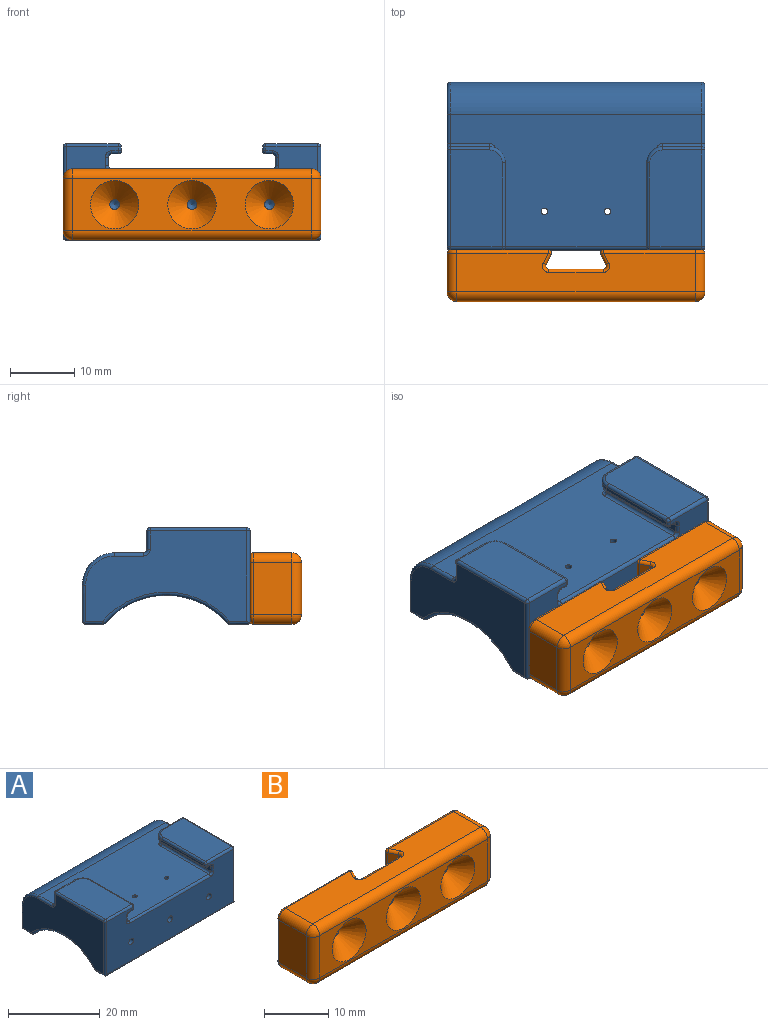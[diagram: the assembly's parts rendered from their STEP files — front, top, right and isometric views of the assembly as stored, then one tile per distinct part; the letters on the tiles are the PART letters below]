
ASSEMBLY  parts=2 mates=1
PART A: 152 faces, bbox 40x26.4x15.3 mm
  f0: cylinder r=2.5mm len=2.5mm, axis (0,0,-1), area 2.6mm2, adj f11,f18,f89,f99,f103
  f1: plane 12.56x0.75mm, normal (0,0,-1), area 9.5mm2, adj f2,f3,f47,f81
  f2: cylinder r=0.5mm len=17.92mm, axis (-1,0,0), area 13.6mm2, adj f1,f4,f26,f41,f42,f47,f49,f83
  f3: cylinder r=0.5mm len=12.56mm, axis (-1,0,0), area 5.8mm2, adj f1,f28,f47,f79
  f4: plane 2.66x0.5mm, normal (0,0,-1), area 1.3mm2, adj f2,f42,f48,f49
  f5: plane 12.56x0.75mm, normal (0,0,-1), area 9.5mm2, adj f43,f44,f46,f78
  f6: plane 2.66x0.5mm, normal (0,0,-1), area 1.3mm2, adj f58,f68,f69,f73
  f7: plane 29x0.75mm, normal (0,0,-1), area 21.8mm2, adj f63,f64,f71,f73
  f8: plane 2.66x0.5mm, normal (0,0,-1), area 1.3mm2, adj f66,f67,f72,f73
  f9: plane 2.66x0.5mm, normal (0,0,-1), area 1.3mm2, adj f40,f44,f45,f50
  f10: cylinder r=12.5mm len=18.92mm, axis (1,0,0), area 107.3mm2, adj f48,f56,f60,f66
  f11: plane 6.05x2.9mm, normal (0,1,0), area 17.5mm2, adj f0,f88,f96,f102,f105
  f12: plane 14.73x1mm, normal (0,0,-1), area 14.2mm2, adj f113,f118,f124,f125
  f13: plane 13x0.6mm, normal (1,0,0), area 7.8mm2, adj f25,f110,f118,f119
  f14: plane 15x8.05mm, normal (0,0,1), area 119.9mm2, adj f119,f120,f126,f130,f131
  f15: plane 25x14mm, normal (-1,0,0), area 245.5mm2, adj f49,f56,f67,f121,f131,f132,f136,f138
  f16: plane 25x14mm, normal (1,0,0), area 245.5mm2, adj f50,f57,f68,f85,f86,f87,f91,f95
  f17: plane 15x8.05mm, normal (0,0,1), area 119.9mm2, adj f87,f88,f89,f93,f94
  f18: plane 13x0.6mm, normal (-1,0,0), area 7.8mm2, adj f0,f93,f100,f101
  f19: plane 14.73x1mm, normal (0,0,-1), area 14.2mm2, adj f99,f100,f106,f107
  f20: plane 15x1.3mm, normal (-1,0,0), area 19.5mm2, adj f105,f106,f111,f112
  f21: plane 39x20.5mm, normal (0,0,1), area 572.8mm2, adj f84,f95,f102,f108,f111,f122,f133,f137
  f22: plane 15x1.3mm, normal (1,0,0), area 19.5mm2, adj f123,f124,f133,f134
  f23: plane 39x14mm, normal (0,-1,0), area 439mm2, adj f73,f85,f94,f101,f107,f109,f110,f112
  f24: plane 6.05x2.9mm, normal (0,1,0), area 17.5mm2, adj f25,f130,f134,f138,f141
  f25: cylinder r=2.5mm len=2.5mm, axis (0,0,1), area 2.6mm2, adj f13,f24,f125,f126,f129
  f26: plane 39x5.6mm, normal (0,1,0), area 214.1mm2, adj f2,f44,f82,f84,f86,f132
  f27: cylinder r=12.5mm len=18.92mm, axis (1,0,0), area 107.3mm2, adj f45,f54,f57,f58
  f28: cylinder r=14mm len=28.19mm, axis (-1,0,0), area 664.9mm2, adj f3,f29,f30,f43,f46,f47,f63,f64
  f29: plane 22.25x5.5mm, normal (-1,0,0), area 24mm2, adj f28,f43,f54,f63
  f30: plane 22.25x5.5mm, normal (1,0,0), area 24mm2, adj f28,f47,f60,f71
  f31: cylinder r=14.75mm len=24.49mm, axis (1,0,0), area 101.2mm2, adj f33,f34,f39,f40,f43,f63,f69,f70
  f32: cylinder r=13.5mm len=20.43mm, axis (1,0,0), area 81.1mm2, adj f33,f34,f45,f58
  f33: plane 24.11x6.25mm, normal (1,0,0), area 32.7mm2, adj f31,f32,f43,f45,f58,f63
  f34: plane 24.11x6.25mm, normal (-1,0,0), area 32.7mm2, adj f31,f32,f40,f45,f58,f69
  f35: cylinder r=14.75mm len=24.49mm, axis (-1,0,0), area 101.2mm2, adj f37,f38,f41,f42,f47,f71,f72,f74
  f36: cylinder r=13.5mm len=20.43mm, axis (-1,0,0), area 81.1mm2, adj f37,f38,f48,f66
  f37: plane 24.11x6.25mm, normal (-1,0,0), area 32.7mm2, adj f35,f36,f47,f48,f66,f71
  f38: plane 24.11x6.25mm, normal (1,0,0), area 32.7mm2, adj f35,f36,f42,f48,f66,f72
  f39: cylinder r=0.5mm len=4.34mm, axis (1,0,0), area 1.6mm2, adj f31,f40,f43,f44
  f40: cylinder r=0.5mm len=2.74mm, axis (0,1,0), area 1.7mm2, adj f9,f31,f34,f39,f44,f45
  f41: cylinder r=0.5mm len=4.34mm, axis (-1,0,0), area 1.6mm2, adj f2,f35,f42,f47
  f42: cylinder r=0.5mm len=2.74mm, axis (0,-1,0), area 1.7mm2, adj f2,f4,f35,f38,f41,f48
  f43: cylinder r=0.5mm len=2.74mm, axis (0,-1,0), area 3mm2, adj f5,f28,f29,f31,f33,f39,f44,f45
  f44: cylinder r=0.5mm len=17.92mm, axis (-1,0,0), area 13.6mm2, adj f5,f9,f26,f39,f40,f43,f50,f80
  f45: cylinder r=0.5mm len=5mm, axis (1,0,0), area 6.4mm2, adj f9,f27,f32,f33,f34,f40,f43,f51
  f46: cylinder r=0.5mm len=12.56mm, axis (-1,0,0), area 5.8mm2, adj f5,f28,f43,f76
  f47: cylinder r=0.5mm len=2.74mm, axis (0,1,0), area 3mm2, adj f1,f2,f3,f28,f30,f35,f37,f41
  f48: cylinder r=0.5mm len=5mm, axis (-1,0,0), area 6.4mm2, adj f4,f10,f36,f37,f38,f42,f47,f52
  f49: cylinder r=0.5mm len=3.02mm, axis (0,1,0), area 2.2mm2, adj f2,f4,f15,f52,f132
  f50: cylinder r=0.5mm len=3.02mm, axis (0,1,0), area 2.2mm2, adj f9,f16,f44,f53,f86
  f51: sphere r=0.5mm, area 0.2mm2, adj f43,f45,f54
  f52: sphere r=0.5mm, area 0.2mm2, adj f48,f49,f56
  f53: sphere r=0.5mm, area 0.2mm2, adj f45,f50,f57
  f54: torus R=13mm, axis (1,0,0), area 17.1mm2, adj f27,f29,f51,f59
  f55: sphere r=0.5mm, area 0.2mm2, adj f47,f48,f60
  f56: torus R=13mm, axis (1,0,0), area 17.1mm2, adj f10,f15,f52,f61
  f57: torus R=13mm, axis (-1,0,0), area 17.1mm2, adj f16,f27,f53,f62
  f58: cylinder r=0.5mm len=5mm, axis (1,0,0), area 6.4mm2, adj f6,f27,f32,f33,f34,f59,f62,f63
  f59: sphere r=0.5mm, area 0.2mm2, adj f54,f58,f63
  f60: torus R=13mm, axis (1,0,0), area 17.1mm2, adj f10,f30,f55,f65
  f61: sphere r=0.5mm, area 0.2mm2, adj f56,f66,f67
  f62: sphere r=0.5mm, area 0.2mm2, adj f57,f58,f68
  f63: cylinder r=0.5mm len=2.74mm, axis (0,1,0), area 3mm2, adj f7,f28,f29,f31,f33,f58,f59,f64
  f64: cylinder r=0.5mm len=29mm, axis (-1,0,0), area 13.5mm2, adj f7,f28,f63,f71
  f65: sphere r=0.5mm, area 0.2mm2, adj f60,f66,f71
  f66: cylinder r=0.5mm len=5mm, axis (1,0,0), area 6.4mm2, adj f8,f10,f36,f37,f38,f61,f65,f71
  f67: cylinder r=0.5mm len=3.02mm, axis (0,1,0), area 2.2mm2, adj f8,f15,f61,f73,f121
  f68: cylinder r=0.5mm len=3.02mm, axis (0,1,0), area 2.2mm2, adj f6,f16,f62,f73,f85
  f69: cylinder r=0.5mm len=2.74mm, axis (0,1,0), area 1.7mm2, adj f6,f31,f34,f58,f70,f73
  f70: cylinder r=0.5mm len=4.34mm, axis (1,0,0), area 1.6mm2, adj f31,f63,f69,f73
  f71: cylinder r=0.5mm len=2.74mm, axis (0,-1,0), area 3mm2, adj f7,f28,f30,f35,f37,f64,f65,f66
  f72: cylinder r=0.5mm len=2.74mm, axis (0,-1,0), area 1.7mm2, adj f8,f35,f38,f66,f73,f74
  f73: cylinder r=0.5mm len=39.71mm, axis (-1,0,0), area 30.2mm2, adj f6,f7,f8,f23,f63,f67,f68,f69
  f74: cylinder r=0.5mm len=4.34mm, axis (-1,0,0), area 1.6mm2, adj f35,f71,f72,f73
  f75: cylinder r=1.5mm len=2.9mm, axis (0,-1,0), area 6.1mm2, adj f77,f78,f81,f82
  f76: sphere r=0.5mm, area 0.2mm2, adj f46,f77,f78
  f77: bspline ~4.01x1.99mm, area 2.8mm2, adj f28,f75,f76,f79
  f78: cylinder r=0.5mm len=0.75mm, axis (0,-1,0), area 0.5mm2, adj f5,f75,f76,f80
  f79: sphere r=0.5mm, area 0.2mm2, adj f3,f77,f81
  f80: sphere r=0.5mm, area 0.3mm2, adj f44,f78,f82
  f81: cylinder r=0.5mm len=0.75mm, axis (0,-1,0), area 0.5mm2, adj f1,f75,f79,f83
  f82: torus R=2mm, axis (0,1,0), area 3.5mm2, adj f26,f75,f80,f83
  f83: sphere r=0.5mm, area 0.3mm2, adj f2,f81,f82
  f84: cylinder r=5mm len=39mm, axis (1,0,0), area 306.3mm2, adj f21,f26,f91,f136
  f85: cylinder r=0.5mm len=14.35mm, axis (0,0,-1), area 11.1mm2, adj f16,f23,f68,f73,f90
  f86: cylinder r=0.5mm len=5.95mm, axis (0,0,-1), area 4.5mm2, adj f16,f26,f44,f50,f91
  f87: cylinder r=0.5mm len=15mm, axis (0,1,0), area 11.8mm2, adj f16,f17,f90,f92
  f88: cylinder r=0.5mm len=6.05mm, axis (-1,0,0), area 4.8mm2, adj f11,f17,f89,f92
  f89: torus R=2mm, axis (0,0,-1), area 2.9mm2, adj f0,f17,f88,f93
  f90: sphere r=0.5mm, area 0.4mm2, adj f85,f87,f94
  f91: torus R=4.5mm, axis (-1,0,0), area 5.9mm2, adj f16,f84,f86,f95
  f92: sphere r=0.5mm, area 0.4mm2, adj f87,f88,f96
  f93: cylinder r=0.5mm len=13mm, axis (0,1,0), area 10.2mm2, adj f17,f18,f89,f97
  f94: cylinder r=0.5mm len=8.05mm, axis (1,0,0), area 6.3mm2, adj f17,f23,f90,f97
  f95: cylinder r=0.5mm len=4.5mm, axis (0,-1,0), area 3.5mm2, adj f16,f21,f91,f98
  f96: cylinder r=0.5mm len=2.9mm, axis (0,0,1), area 2.3mm2, adj f11,f16,f92,f98
  f97: sphere r=0.5mm, area 0.4mm2, adj f93,f94,f101
  f98: torus R=1mm, axis (-1,0,0), area 0.8mm2, adj f16,f95,f96,f102
  f99: torus R=2mm, axis (0,0,1), area 1.9mm2, adj f0,f19,f100,f103
  f100: cylinder r=0.5mm len=13mm, axis (0,1,0), area 10.2mm2, adj f18,f19,f99,f104
  f101: cylinder r=0.5mm len=0.6mm, axis (0,0,1), area 0.5mm2, adj f18,f23,f97,f104
  f102: cylinder r=0.5mm len=6.05mm, axis (1,0,0), area 4.8mm2, adj f11,f21,f98,f108
  f103: bspline ~1.36x1.22mm, area 1mm2, adj f0,f99,f105,f106
  f104: sphere r=0.5mm, area 0.4mm2, adj f100,f101,f107
  f105: cylinder r=0.5mm len=1.3mm, axis (0,0,-1), area 1mm2, adj f11,f20,f103,f108
  f106: cylinder r=0.5mm len=15mm, axis (0,-1,0), area 11.7mm2, adj f19,f20,f103,f109
  f107: cylinder r=0.5mm len=1mm, axis (-1,0,0), area 0.8mm2, adj f19,f23,f104,f109
  f108: torus R=1mm, axis (0,0,-1), area 0.8mm2, adj f21,f102,f105,f111
  f109: torus R=1mm, axis (0,-1,0), area 0.8mm2, adj f23,f106,f107,f112
  f110: cylinder r=0.5mm len=0.6mm, axis (0,0,-1), area 0.5mm2, adj f13,f23,f114,f115
  f111: cylinder r=0.5mm len=15mm, axis (0,-1,0), area 11.8mm2, adj f20,f21,f108,f116
  f112: cylinder r=0.5mm len=1.3mm, axis (0,0,1), area 1mm2, adj f20,f23,f109,f116
  f113: cylinder r=0.5mm len=1mm, axis (-1,0,0), area 0.8mm2, adj f12,f23,f114,f117
  f114: sphere r=0.5mm, area 0.4mm2, adj f110,f113,f118
  f115: sphere r=0.5mm, area 0.4mm2, adj f110,f119,f120
  f116: torus R=1mm, axis (0,-1,0), area 0.8mm2, adj f23,f111,f112,f122
  f117: torus R=1mm, axis (0,-1,0), area 0.8mm2, adj f23,f113,f123,f124
  f118: cylinder r=0.5mm len=13mm, axis (0,1,0), area 10.2mm2, adj f12,f13,f114,f125
  f119: cylinder r=0.5mm len=13mm, axis (0,1,0), area 10.2mm2, adj f13,f14,f115,f126
  f120: cylinder r=0.5mm len=8.05mm, axis (1,0,0), area 6.3mm2, adj f14,f23,f115,f127
  f121: cylinder r=0.5mm len=14.35mm, axis (0,0,1), area 11.1mm2, adj f15,f23,f67,f73,f127
  f122: cylinder r=0.5mm len=24.9mm, axis (1,0,0), area 19.6mm2, adj f21,f23,f116,f128
  f123: cylinder r=0.5mm len=1.3mm, axis (0,0,-1), area 1mm2, adj f22,f23,f117,f128
  f124: cylinder r=0.5mm len=15mm, axis (0,-1,0), area 11.7mm2, adj f12,f22,f117,f129
  f125: torus R=2mm, axis (0,0,1), area 1.9mm2, adj f12,f25,f118,f129
  f126: torus R=2mm, axis (0,0,-1), area 2.9mm2, adj f14,f25,f119,f130
  f127: sphere r=0.5mm, area 0.4mm2, adj f120,f121,f131
  f128: torus R=1mm, axis (0,-1,0), area 0.8mm2, adj f23,f122,f123,f133
  f129: bspline ~1.6x1.08mm, area 1mm2, adj f25,f124,f125,f134
  f130: cylinder r=0.5mm len=6.05mm, axis (-1,0,0), area 4.8mm2, adj f14,f24,f126,f135
  f131: cylinder r=0.5mm len=15mm, axis (0,1,0), area 11.8mm2, adj f14,f15,f127,f135
  f132: cylinder r=0.5mm len=5.95mm, axis (0,0,1), area 4.5mm2, adj f2,f15,f26,f49,f136
  f133: cylinder r=0.5mm len=15mm, axis (0,-1,0), area 11.8mm2, adj f21,f22,f128,f137
  f134: cylinder r=0.5mm len=1.3mm, axis (0,0,1), area 1mm2, adj f22,f24,f129,f137
  f135: sphere r=0.5mm, area 0.4mm2, adj f130,f131,f138
  f136: torus R=4.5mm, axis (1,0,0), area 5.9mm2, adj f15,f84,f132,f139
  f137: torus R=1mm, axis (0,0,-1), area 0.8mm2, adj f21,f133,f134,f141
  f138: cylinder r=0.5mm len=2.9mm, axis (0,0,-1), area 2.3mm2, adj f15,f24,f135,f140
  f139: cylinder r=0.5mm len=4.5mm, axis (0,-1,0), area 3.5mm2, adj f15,f21,f136,f140
  f140: torus R=1mm, axis (1,0,0), area 0.8mm2, adj f15,f138,f139,f141
  f141: cylinder r=0.5mm len=6.05mm, axis (1,0,0), area 4.8mm2, adj f21,f24,f137,f140
  f142: cylinder r=0.5mm len=5.73mm, axis (0,0,1), area 12.1mm2, adj f21,f145
  f143: cylinder r=0.5mm len=5.73mm, axis (0,0,1), area 12.1mm2, adj f21,f144
  f144: bspline ~7.01x5.77mm, area 44.9mm2, adj f28,f143
  f145: bspline ~7.01x5.77mm, area 44.9mm2, adj f28,f142
  f146: cone r=0mm half-angle=59deg, axis (0,-1,0), area 2.1mm2, adj f147
  f147: cylinder r=0.75mm len=7mm, axis (0,-1,0), area 33mm2, adj f23,f146
  f148: cone r=0mm half-angle=59deg, axis (0,-1,0), area 2.1mm2, adj f149
  f149: cylinder r=0.75mm len=7mm, axis (0,-1,0), area 33mm2, adj f23,f148
  f150: cone r=0mm half-angle=59deg, axis (0,-1,0), area 2.1mm2, adj f151
  f151: cylinder r=0.75mm len=7mm, axis (0,-1,0), area 33mm2, adj f23,f150
PART B: 59 faces, bbox 40.2x8x11.3 mm
  f0: plane 8.1x6mm, normal (-1,0,0), area 48.6mm2, adj f13,f17,f18,f50
  f1: plane 15.19x10.1mm, normal (0,1,0), area 148.1mm2, adj f45,f46,f48,f50,f51,f52,f55
  f2: plane 37x8.1mm, normal (0,-1,0), area 167.2mm2, adj f16,f17,f21,f22,f56,f57,f58
  f3: plane 15.19x10.1mm, normal (0,1,0), area 148.1mm2, adj f25,f26,f27,f29,f31,f32,f54
  f4: plane 37x6mm, normal (0,0,1), area 192.8mm2, adj f18,f22,f24,f32,f37,f39,f42,f44
  f5: plane 37x6mm, normal (0,0,-1), area 192.8mm2, adj f13,f15,f16,f26,f30,f33,f35,f38
  f6: plane 8.1x6mm, normal (1,0,0), area 48.6mm2, adj f15,f21,f24,f27
  f7: cylinder r=0.75mm len=4.5mm, axis (0,1,0), area 21.2mm2, adj f55,f56
  f8: cylinder r=0.75mm len=1.5mm, axis (0,1,0), area 7.1mm2, adj f53,f57
  f9: cylinder r=0.75mm len=4.5mm, axis (0,1,0), area 21.2mm2, adj f54,f58
  f10: plane 10.1x8.38mm, normal (0,1,0), area 79.7mm2, adj f35,f36,f41,f42,f53
  f11: plane 10.1x1.55mm, normal (0.89,-0.45,0), area 17.5mm2, adj f40,f41,f46,f47
  f12: plane 10.1x1.55mm, normal (-0.89,-0.45,0), area 17.5mm2, adj f30,f31,f36,f37
  f13: cylinder r=1.5mm len=6mm, axis (0,1,0), area 14.1mm2, adj f0,f5,f14,f48
  f14: sphere r=1.5mm, area 3.5mm2, adj f13,f16,f17
  f15: cylinder r=1.5mm len=6mm, axis (0,1,0), area 14.1mm2, adj f5,f6,f19,f25
  f16: cylinder r=1.5mm len=37mm, axis (-1,0,0), area 87.2mm2, adj f2,f5,f14,f19
  f17: cylinder r=1.5mm len=8.1mm, axis (0,0,1), area 19.1mm2, adj f0,f2,f14,f20
  f18: cylinder r=1.5mm len=6mm, axis (0,-1,0), area 14.1mm2, adj f0,f4,f20,f52
  f19: sphere r=1.5mm, area 3.5mm2, adj f15,f16,f21
  f20: sphere r=1.5mm, area 3.5mm2, adj f17,f18,f22
  f21: cylinder r=1.5mm len=8.1mm, axis (0,0,-1), area 19.1mm2, adj f2,f6,f19,f23
  f22: cylinder r=1.5mm len=37mm, axis (1,0,0), area 87.2mm2, adj f2,f4,f20,f23
  f23: sphere r=1.5mm, area 3.5mm2, adj f21,f22,f24
  f24: cylinder r=1.5mm len=6mm, axis (0,-1,0), area 14.1mm2, adj f4,f6,f23,f29
  f25: torus R=1mm, axis (0,-1,0), area 1.6mm2, adj f3,f15,f26,f27
  f26: cylinder r=0.5mm len=14.19mm, axis (1,0,0), area 11.1mm2, adj f3,f5,f25,f28
  f27: cylinder r=0.5mm len=8.1mm, axis (0,0,1), area 6.4mm2, adj f3,f6,f25,f29
  f28: sphere r=0.5mm, area 0.5mm2, adj f26,f30,f31
  f29: torus R=1mm, axis (0,-1,0), area 1.6mm2, adj f3,f24,f27,f32
  f30: cylinder r=0.5mm len=1.78mm, axis (-0.45,0.89,0), area 1.4mm2, adj f5,f12,f28,f33
  f31: cylinder r=0.5mm len=10.1mm, axis (0,0,1), area 10.3mm2, adj f3,f12,f28,f34
  f32: cylinder r=0.5mm len=14.19mm, axis (-1,0,0), area 11.1mm2, adj f3,f4,f29,f34
  f33: torus R=1mm, axis (0,0,1), area 1.1mm2, adj f5,f30,f35,f36
  f34: sphere r=0.5mm, area 0.5mm2, adj f31,f32,f37
  f35: cylinder r=0.5mm len=8.38mm, axis (1,0,0), area 6.6mm2, adj f5,f10,f33,f38
  f36: cylinder r=0.5mm len=10.1mm, axis (0,0,-1), area 10.3mm2, adj f10,f12,f33,f39
  f37: cylinder r=0.5mm len=1.78mm, axis (-0.45,0.89,0), area 1.4mm2, adj f4,f12,f34,f39
  f38: torus R=1mm, axis (0,0,1), area 1.1mm2, adj f5,f35,f40,f41
  f39: torus R=1mm, axis (0,0,-1), area 1.1mm2, adj f4,f36,f37,f42
  f40: cylinder r=0.5mm len=1.78mm, axis (-0.45,-0.89,0), area 1.4mm2, adj f5,f11,f38,f43
  f41: cylinder r=0.5mm len=10.1mm, axis (0,0,-1), area 10.3mm2, adj f10,f11,f38,f44
  f42: cylinder r=0.5mm len=8.38mm, axis (1,0,0), area 6.6mm2, adj f4,f10,f39,f44
  f43: sphere r=0.5mm, area 0.5mm2, adj f40,f45,f46
  f44: torus R=1mm, axis (0,0,-1), area 1.1mm2, adj f4,f41,f42,f47
  f45: cylinder r=0.5mm len=14.19mm, axis (1,0,0), area 11.1mm2, adj f1,f5,f43,f48
  f46: cylinder r=0.5mm len=10.1mm, axis (0,0,-1), area 10.3mm2, adj f1,f11,f43,f49
  f47: cylinder r=0.5mm len=1.78mm, axis (-0.45,-0.89,0), area 1.4mm2, adj f4,f11,f44,f49
  f48: torus R=1mm, axis (0,-1,0), area 1.6mm2, adj f1,f13,f45,f50
  f49: sphere r=0.5mm, area 0.5mm2, adj f46,f47,f51
  f50: cylinder r=0.5mm len=8.1mm, axis (0,0,-1), area 6.4mm2, adj f0,f1,f48,f52
  f51: cylinder r=0.5mm len=14.19mm, axis (-1,0,0), area 11.1mm2, adj f1,f4,f49,f52
  f52: torus R=1mm, axis (0,-1,0), area 1.6mm2, adj f1,f18,f50,f51
  f53: torus R=1.25mm, axis (0,-1,0), area 4.6mm2, adj f8,f10
  f54: torus R=1.25mm, axis (0,-1,0), area 4.6mm2, adj f3,f9
  f55: torus R=1.25mm, axis (0,-1,0), area 4.6mm2, adj f1,f7
  f56: cone r=0.75mm half-angle=45deg, axis (0,-1,0), area 60mm2, adj f2,f7
  f57: cone r=0.75mm half-angle=45deg, axis (0,-1,0), area 60mm2, adj f2,f8
  f58: cone r=0.75mm half-angle=45deg, axis (0,-1,0), area 60mm2, adj f2,f9
PLACE A t=(0.07,-0.03,-1.47)mm
PLACE B t=(0.53,-16.03,9.52)mm
MATE cylindrical A.f146 <-> B.f9  axis (0,-1,0) through (12.07,-16.03,4.08)mm
